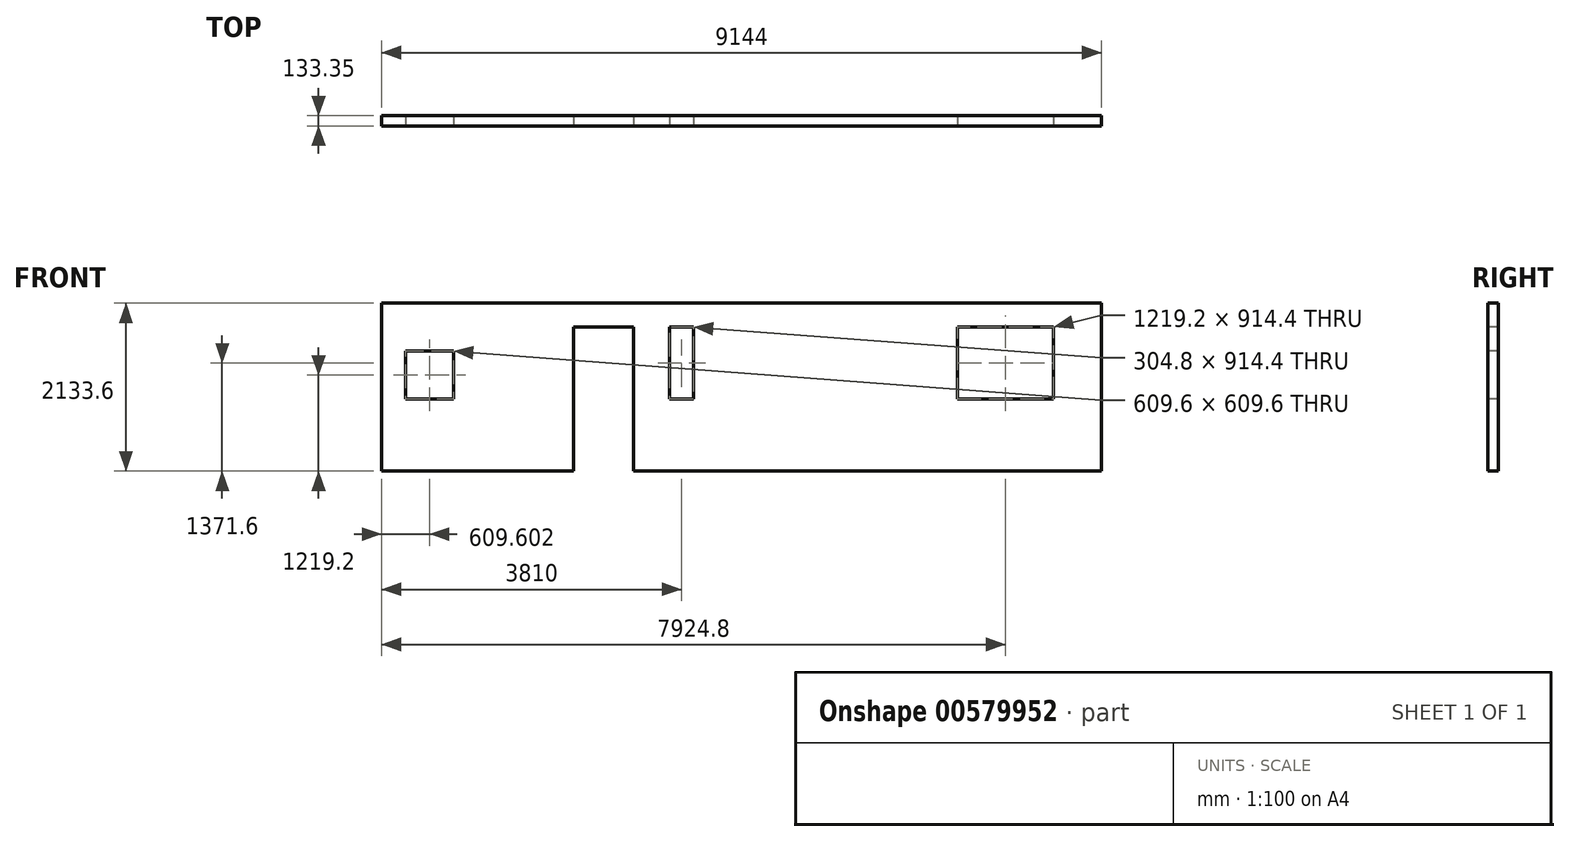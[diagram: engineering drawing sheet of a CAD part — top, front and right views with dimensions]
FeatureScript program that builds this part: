
annotation { "Feature Type Name" : "Feature", "Feature Type Description" : "" }
export const myFeature = defineFeature(function(context is Context, id is Id, definition is map)
    precondition{}
    {
        {
            var Q0;
            Q0=qCreatedBy(makeId("Front.planeOp"),FACE);
            var sketch = newSketch(context, id + "F0", { "sketchPlane" : qUnion([Q0])});
            skLineSegment(sketch, "E0.bottom", {"start": v(-382.47, 2018.22) * mm, "end": v(8761.53, 2018.22) * mm});
            skLineSegment(sketch, "E0.top", {"start": v(-382.47, -115.38) * mm, "end": v(8761.53, -115.38) * mm});
            skLineSegment(sketch, "E0.left", {"start": v(-382.47, 2018.22) * mm, "end": v(-382.47, -115.38) * mm});
            skLineSegment(sketch, "E0.right", {"start": v(8761.53, 2018.22) * mm, "end": v(8761.53, -115.38) * mm});
            skSolve(sketch);
        }
        {
            var Q0;
            Q0=makeQuery(id+"F0.imprint","IMPRINT",FACE,{"disambiguationData":[TD([[makeQuery(id+"F0.imprint","IMPRINT",EDGE,{"derivedFrom":sQuery(id+"F0.wireOp",EDGE,"E0.bottom")}),-1.0]])]});
            extrude(context, id + "F1", {"entities" : qUnion([Q0]), "depth" : 133.35 * mm, "offsetDistance" : 25.4 * mm});
        }
        {
            var Q0;
            Q0=makeQuery(id+"F1.opExtrude","CAP_FACE",FACE,{"disambiguationData":[OSD([sQuery(id+"F0.wireOp",EDGE,"E0.bottom"),sQuery(id+"F0.wireOp",EDGE,"E0.top"),sQuery(id+"F0.wireOp",EDGE,"E0.left"),sQuery(id+"F0.wireOp",EDGE,"E0.right")])],"isStart":false});
            var sketch = newSketch(context, id + "F2", { "sketchPlane" : qUnion([Q0])});
            skLineSegment(sketch, "E1.bottom", {"start": v(-77.67, 1408.62) * mm, "end": v(531.93, 1408.62) * mm});
            skLineSegment(sketch, "E1.top", {"start": v(-77.67, 799.02) * mm, "end": v(531.93, 799.02) * mm});
            skLineSegment(sketch, "E1.left", {"start": v(-77.67, 1408.62) * mm, "end": v(-77.67, 799.02) * mm});
            skLineSegment(sketch, "E1.right", {"start": v(531.93, 1408.62) * mm, "end": v(531.93, 799.02) * mm});
            skLineSegment(sketch, "E2.bottom", {"start": v(2055.93, -115.38) * mm, "end": v(2817.93, -115.38) * mm});
            skLineSegment(sketch, "E2.top", {"start": v(2055.93, 1713.42) * mm, "end": v(2817.93, 1713.42) * mm});
            skLineSegment(sketch, "E2.left", {"start": v(2055.93, -115.38) * mm, "end": v(2055.93, 1713.42) * mm});
            skLineSegment(sketch, "E2.right", {"start": v(2817.93, -115.38) * mm, "end": v(2817.93, 1713.42) * mm});
            skLineSegment(sketch, "E3.bottom", {"start": v(3275.13, 1713.42) * mm, "end": v(3579.93, 1713.42) * mm});
            skLineSegment(sketch, "E3.top", {"start": v(3275.13, 799.02) * mm, "end": v(3579.93, 799.02) * mm});
            skLineSegment(sketch, "E3.left", {"start": v(3275.13, 1713.42) * mm, "end": v(3275.13, 799.02) * mm});
            skLineSegment(sketch, "E3.right", {"start": v(3579.93, 1713.42) * mm, "end": v(3579.93, 799.02) * mm});
            skLineSegment(sketch, "E4.bottom", {"start": v(6932.73, 1713.42) * mm, "end": v(8151.93, 1713.42) * mm});
            skLineSegment(sketch, "E4.top", {"start": v(6932.73, 799.02) * mm, "end": v(8151.93, 799.02) * mm});
            skLineSegment(sketch, "E4.left", {"start": v(6932.73, 1713.42) * mm, "end": v(6932.73, 799.02) * mm});
            skLineSegment(sketch, "E4.right", {"start": v(8151.93, 1713.42) * mm, "end": v(8151.93, 799.02) * mm});
            skSolve(sketch);
        }
        {
            var Q0;
            Q0 = qSketchRegion(id + "F2", true);
            extrude(context, id + "F3", {"entities" : qUnion([Q0]), "operationType" : NewBodyOperationType.REMOVE, "oppositeDirection" : true, "depth" : 133.35 * mm, "offsetDistance" : 25.4 * mm});
        }
    });
